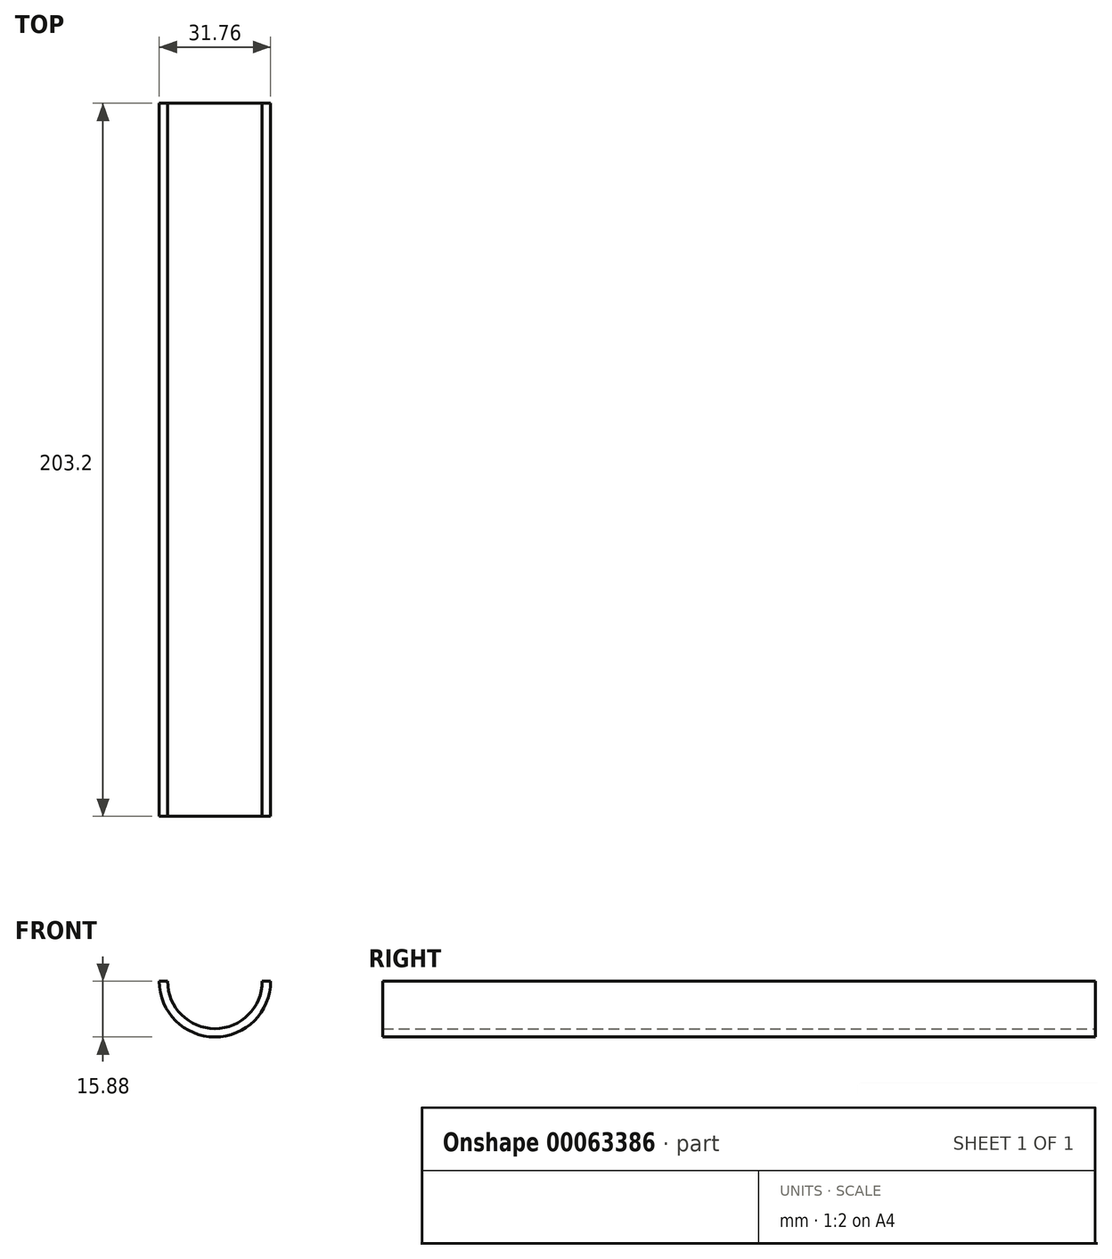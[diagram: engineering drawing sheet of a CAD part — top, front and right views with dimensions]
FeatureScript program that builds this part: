
annotation { "Feature Type Name" : "Feature", "Feature Type Description" : "" }
export const myFeature = defineFeature(function(context is Context, id is Id, definition is map)
    precondition{}
    {
        {
            var Q0;
            Q0=qCreatedBy(makeId("Front.planeOp"),FACE);
            var sketch = newSketch(context, id + "F0", { "sketchPlane" : qUnion([Q0])});
            skArc(sketch, "E0", {"start": v(-13.5, 0) * mm, "mid": v(0, -13.5) * mm, "end": v(13.5, 0) * mm});
            skArc(sketch, "E1", {"start": v(-15.88, 0) * mm, "mid": v(0, -15.88) * mm, "end": v(15.88, 0) * mm});
            skLineSegment(sketch, "E2", {"start": v(-15.88, 0) * mm, "end": v(-13.5, 0) * mm});
            skLineSegment(sketch, "E3", {"start": v(13.5, 0) * mm, "end": v(15.88, 0) * mm});
            skSolve(sketch);
        }
        {
            var Q0;
            Q0=qSketchRegion(id+"F0",true);
            extrude(context, id + "F1", {"entities" : qUnion([Q0]), "endBound" : BoundingType.SYMMETRIC, "depth" : 203.2 * mm});
        }
    });
